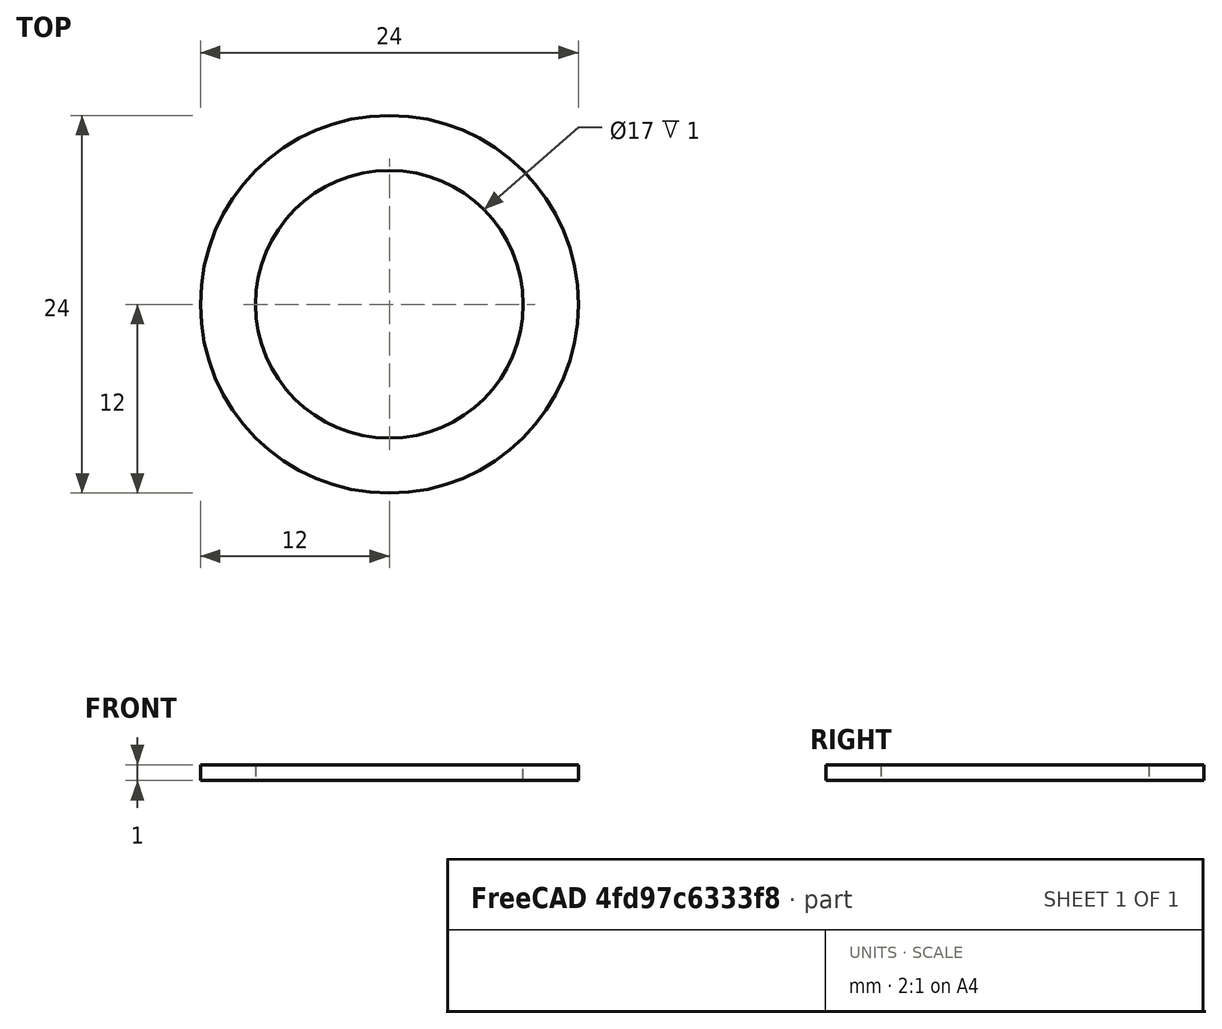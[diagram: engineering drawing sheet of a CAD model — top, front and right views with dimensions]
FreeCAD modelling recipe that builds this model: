
FCSTD DOCUMENT  (FreeCAD 0.19R24276 (Git))
Label: Ring_d17_d24
License: All rights reserved
LicenseURL: http://en.wikipedia.org/wiki/All_rights_reserved
objects: Sketcher::SketchObject×1, PartDesign::Pad×1, PartDesign::Body×1
note: 4 computed .brp shape members not serialized (recipe doc carries the construction recipe); baked Part::Feature solids carry a one-line shape summary decoded from their .brp

FEATURE [Sketcher::SketchObject] Sketch
  FullyConstrained = true
  MapMode = 5
  Support = -> [XY_Plane]
  sketch-geometry (2):
    g0: Circle CenterX=0 CenterY=0 CenterZ=0 NormalX=0 NormalY=0 NormalZ=1 AngleXU=0 Radius=12
    g1: Circle CenterX=0 CenterY=0 CenterZ=0 NormalX=0 NormalY=0 NormalZ=1 AngleXU=0 Radius=8.5
  constraints (4):
    c: Coincident(g0,g-1)
    c: Coincident(g1,g-1)
    c: Diameter(g0) = 24
    c: Diameter(g1) = 17
FEATURE [PartDesign::Pad] Pad
  Direction = (1,1,1)
  Length = 1
  Length2 = 100
  Profile = -> Sketch
  Type = 0
FEATURE [PartDesign::Body] Body
  Group = -> [Sketch,Pad]
  Origin = -> Origin
  Tip = -> Pad
